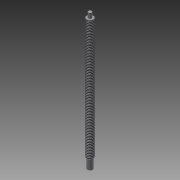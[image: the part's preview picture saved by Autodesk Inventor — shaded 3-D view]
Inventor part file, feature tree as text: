
AUTODESK INVENTOR PART (.ipt)
format: ipt  version: 2013 (Build 170138000, 138)  size: 83,968 bytes
history: native  units: in
note: dims shown in document units (in); Inventor stores cm internally (conversion verified against a paired STEP export)
features: extrude x3, sketch x3, thread x1
ambient origin geometry x8: Origin, YZ Plane, XZ Plane, XY Plane, X Axis, Y Axis, Z Axis, Center Point
bodies: Solid1 (feature_tree)
feature tree (7):
  extrude  "Extrusion1"  Depth=10.0in TaperAngle=0.0deg
  thread  "Thread1"  [1 undecoded]
  extrude  "Extrusion2"  Depth=0.105in
  extrude  "Extrusion3"  Depth=0.3937in
  sketch  "Sketch1"  dims[d0=0.5in d1=10.0in d2=0.0in d3=1.0in d4=0.0in]
  sketch  "Sketch2"  dims[d5=0.25in d6=0.105in]
  sketch  "Sketch3"  dims[d7=0.375in d8=0.0in d9=0.3937in d10=0.75in d11=0.0in]
note: 1 required parameter value undecoded (feature->parameter linkage not recoverable at this tier; creation-order binding heuristic only, values carry confidence <= 0.55)
